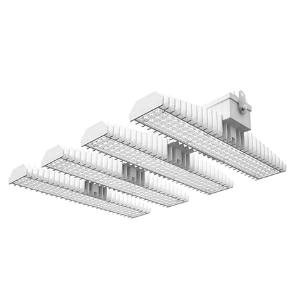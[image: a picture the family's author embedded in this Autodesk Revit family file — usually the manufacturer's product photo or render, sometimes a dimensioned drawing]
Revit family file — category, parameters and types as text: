
# Revit family: 3f_filippi_-_3f_lem_ampio_3f_filippi_-_59160_a0811_-_3f_lem_4_led_200-865_cr_ampio___vt_bec6
name_source: partatom
category: Lighting Fixtures
units: mm (PartAtom-declared; Revit-internal decimal feet)

## family parameters
Cut with Voids When Loaded = No
Host = Face
Light Source = No
Part Type = Normal
Room Calculation Point = No
Round Connector Dimension = Use Diameter
Shared = No

## types (1)
- 3F Filippi - 3F LEM Ampio (1 x LED, 31641 lm, 218 W, 6500 K)
    Apparent Load = 218 VA
    Approval mark = CE
    CIE Flux Codes = 60 92 99 100 100
    Color Rendering = 80
    Color Temperature = 6500 K
    Control Gear = Electronic ballast
    Default Elevation = 1800 mm
    Description = Industrial luminaire with high light output and high luminous efficiency designed with the most innovative technologies for environments with temperature up to 55°C.

ILLUMINOTECHNICAL
Luminous efficiency 100% (DLOR 99%, ULOR 1%).
Initial luminous flux of the luminaire 31641 lm.
Direct symmetric wide distribution: the illuminated area has a rectangular shape.
Installation Interdistance Transv.D = 1.58 x hu - Long.D = 1.45 x hu.
Tabular UGR (CIE 117 - 4H-8H; S=0.25H; 70/50/20): RUG 22.9 - 23.9.
Beam angle: 93° - 99°.
Luminous efficacy 145 lm/W.
Lifetime (L93/B10): 30000 h. (tq+25°C)
Lifetime (L90/B10): 50000 h. (tq+25°C)
Lifetime (L85/B10): 80000 h. (tq+25°C)
Lifetime (L80/B10): 100000 h. (tq+25°C)
Lifetime (L85/B10): 50000 h. (tq+55°C)
Sudden decreased luminous flux after 50000 hours: 0% (C0).
Photobiological safety in compliance with IEC/TR 62778: RG0 risk exempt, (IEC 62471).
In compliance with IEC/EN 62722-2-1 - IEC/EN 62717 standards.

SOURCE
4 Mid-Power linear LED modules 50W/865.
Energy efficiency class (UE 2019/2020 - UE 2019/2015): C.
CIE 13.3 Colour rendering index: CRI >80 (R9 <50%).
IES TM-30 Fidelity Index: Rf = 84 Rg = 95.
CCT nominal colour temperature 6500 K.
Colour initial tolerance (MacAdam): SDCM 3.

MECHANICAL
Passive modular heatsinks in die-casted aluminium, painted in white colour.
To optimize the thermal management of the LED module, the heatsinks are oversized and provided with self-cleaning of cooling fins.
Wiring body in aluminium and galvanised steel anchored solidly to the sinks and thermally separated.
3F Lens lenses with high luminous efficiency, transparent methacrylate (PMMA), fixed to the LED modules.
Fixing brackets in stainless steel.
Luminaire with limited surface temperature. - D - (EN 60598-2-24)
Dimensions: 757x542 mm, height 133 mm. Weight 19.168 kg.
IP65 protection degree.
Mechanical strength to impacts IK06 (1 joule).
Glow-wire test resistance 650°C.

ELECTRICAL
Halogen Free electronic wiring 230V-50/60Hz, power factor 0.97, THD <25%, constant output current, class I, 2 driver.
Power of the luminaire 218 W.
ENEC - CE.
SAFE FLICKER: PstLM=<1 and SVM=<0.4 (IEC TR 61547-1 and IEC TR 63158), to ensure a more comfortable and safe light.
Luminaire compliant with EN 60598-2-22 for power supply from a centralised emergency system CPSS (Central Power Supply System), not incorporated in the luminaire - high risk areas excluded. The default power and flux are 100% in AC and 100% in DC.
Ambient temperature from -30°C to +55°C.
Temperature class T6 max 85°C.
Quick connection via M20 3P connector with 9-13 mm tightening range.
Power unit positioned on a separate compartment by the LED module to ensure optimum temperatures of cabling components, to be inspectable and maintainable.
Relative humidity UR: <85%.

INSTALLATION
Ceiling / Suspended / Wall.
All accessories dedicated to this product are available on the Catalog and on our website www.3F-Filippi.com.

ACCESSORIES
A0811 - VT transparent glass, tempered, not flammable, with sealing gasket.
One required for each light module. The pack contains 10 pieces.

APPLICATIONS
In commercial environments, exhibition and industrial areas, stores, open areas.
Applications with high ambient temperature up to 55°C.
Environments in which it is necessary a total protection against falling fragments (eg environments with foodstuffs or machines with moving parts or with extreme temperature changes), use luminaires with polycarbonate lenses.

WARNING
Fixture not suitable for cold stores with an ambient temperature <0°C and/or relative humidity >85%.
Luminaire designed for disposal/recycling at end-of-life.
Replaceable (LED only) light source by a professional. Replaceable control gear by a professional.
    Height = 133 mm  [stored 0.436352 ft]
    Lamp = 1 x LED
    Lamp Light Flux = 31641 lm
    Lamp Power = 218 W
    Lamp count = 1
    Length = 757 mm
    Lifetime = 50000 h
    Luminous efficacy = 145 lm/W
    Manufacturer = 3F Filippi
    ModVariant = No
    Model = 3F Filippi - 59160+A0811 - 3F LEM 4 LED 200-865 CR AMPIO + VT
    Mounting Place = Ceiling
    Mounting Type = Pendant
    Number of Poles = 1
    OnlyDefault = Yes
    Power Factor = 1
    Product Name = 3F Filippi - 3F LEM Ampio
    Product group = pendant luminaire
    ProductGroupID = 9
    Protection Class = Protection class I
    Protection Degree = IP 65
    RLX_Detail_Level = 1
    RLX_Emergency_Light_Flux = 0 lm
    RLX_Emergency_Type = 0
    RLX_Emergency_Type_DB = No
    RlxData = <blob elided: 118201 chars, md5=f11ee7a0>
    Socket = socket
    Standby Power = 0 W
    System Light Flux = 31641 lm
    System Power = 218 W
    Type Comments = Product without accessories
    Type Image = 3f_filippi_-_lem_4__a0811.jpg
    URL = http://relux.com
    VarID = ---
    Voltage = 0 V
    Weight = 0.00 kg
    Width = 542 mm

note: [stored X ft] marks values corroborated as IEEE doubles in the binary element streams (Revit-internal decimal feet)

## geometry (parser evidence)
native form markers: Blend x4, Sweep x12
no freeform markers — native parametric forms only
